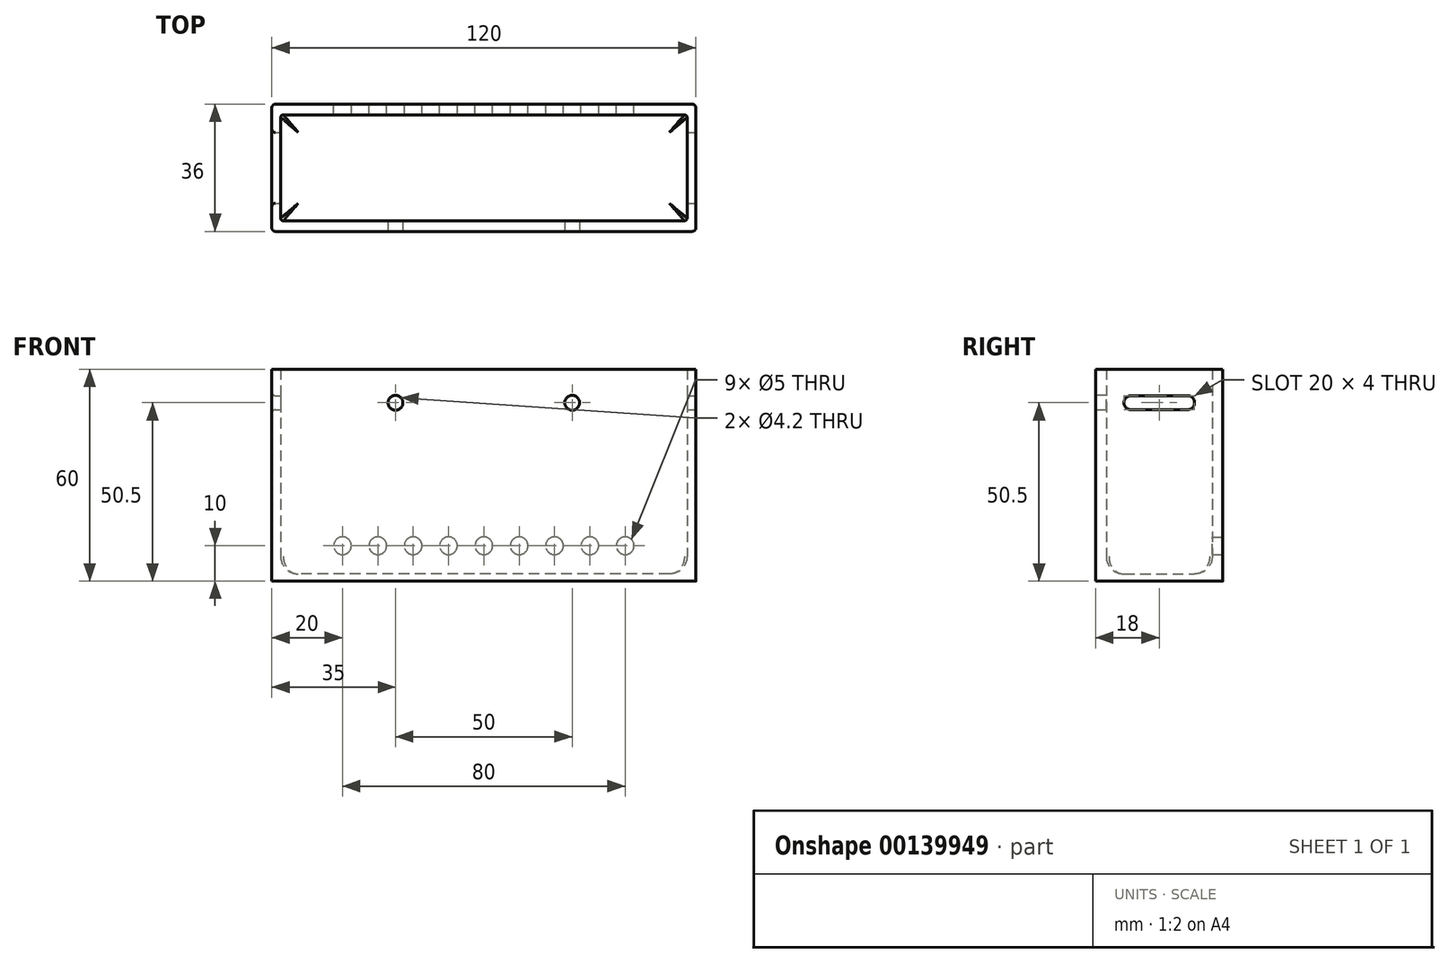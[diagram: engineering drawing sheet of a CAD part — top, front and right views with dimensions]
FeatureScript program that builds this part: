
annotation { "Feature Type Name" : "Feature", "Feature Type Description" : "" }
export const myFeature = defineFeature(function(context is Context, id is Id, definition is map)
    precondition{}
    {
        {
            var Q0;
            Q0=qCreatedBy(makeId("Top.planeOp"),FACE);
            var sketch = newSketch(context, id + "F0", { "sketchPlane" : qUnion([Q0])});
            skLineSegment(sketch, "E0.bottom", {"start": v(0, 0) * mm, "end": v(-115, 0) * mm});
            skLineSegment(sketch, "E0.top", {"start": v(0, 30) * mm, "end": v(-115, 30) * mm});
            skLineSegment(sketch, "E0.left", {"start": v(0, 0) * mm, "end": v(0, 30) * mm});
            skLineSegment(sketch, "E0.right", {"start": v(-115, 0) * mm, "end": v(-115, 30) * mm});
            skLineSegment(sketch, "E1.bottom", {"start": v(-117.5, 33) * mm, "end": v(2.5, 33) * mm});
            skLineSegment(sketch, "E1.top", {"start": v(-117.5, -3) * mm, "end": v(2.5, -3) * mm});
            skLineSegment(sketch, "E1.left", {"start": v(-117.5, 33) * mm, "end": v(-117.5, -3) * mm});
            skLineSegment(sketch, "E1.right", {"start": v(2.5, 33) * mm, "end": v(2.5, -3) * mm});
            skSolve(sketch);
        }
        {
            var Q0;
            Q0=makeQuery(id+"F0.imprint","IMPRINT",FACE,{"disambiguationData":[TD([[makeQuery(id+"F0.imprint","IMPRINT",EDGE,{"derivedFrom":sQuery(id+"F0.wireOp",EDGE,"E0.bottom")}),1.0]])]});
            extrude(context, id + "F1", {"entities" : qUnion([Q0]), "depth" : 60 * mm, "offsetDistance" : 25 * mm});
        }
        {
            var Q0;
            Q0=makeQuery(id+"F0.imprint","IMPRINT",FACE,{"disambiguationData":[TD([[makeQuery(id+"F0.imprint","IMPRINT",EDGE,{"derivedFrom":sQuery(id+"F0.wireOp",EDGE,"E0.bottom")}),-1.0]])]});
            extrude(context, id + "F2", {"entities" : qUnion([Q0]), "operationType" : NewBodyOperationType.ADD, "depth" : 2 * mm, "offsetDistance" : 25 * mm});
        }
        {
            var Q0;
            Q0=makeQuery(id+"F1.opExtrude","SWEPT_FACE",FACE,{"disambiguationData":[OSD([sQuery(id+"F0.wireOp",EDGE,"E1.right")])]});
            var sketch = newSketch(context, id + "F3", { "sketchPlane" : qUnion([Q0])});
            skArc(sketch, "E2", {"start": v(23, 48.5) * mm, "mid": v(25, 50.5) * mm, "end": v(23, 52.5) * mm});
            skArc(sketch, "E3", {"start": v(7, 52.5) * mm, "mid": v(5, 50.5) * mm, "end": v(7, 48.5) * mm});
            skLineSegment(sketch, "E4", {"start": v(23, 52.5) * mm, "end": v(7, 52.5) * mm});
            skLineSegment(sketch, "E5", {"start": v(23, 48.5) * mm, "end": v(7, 48.5) * mm});
            skSolve(sketch);
        }
        {
            var Q0;
            Q0 = qSketchRegion(id + "F3", true);
            extrude(context, id + "F4", {"entities" : qUnion([Q0]), "operationType" : NewBodyOperationType.REMOVE, "oppositeDirection" : true, "depth" : 200 * mm, "offsetDistance" : 25 * mm});
        }
        {
            var Q0;
            Q0=makeQuery(id+"F1.opExtrude","SWEPT_FACE",FACE,{"disambiguationData":[OSD([sQuery(id+"F0.wireOp",EDGE,"E1.bottom")])]});
            var sketch = newSketch(context, id + "F5", { "sketchPlane" : qUnion([Q0])});
            skCircle(sketch, "E6", {"center": v(17.5, 10) * mm, "radius": 2.5 * mm});
            skCircle(sketch, "E7.1.0.0", {"center": v(27.5, 10) * mm, "radius": 2.5 * mm});
            skCircle(sketch, "E7.2.0.0", {"center": v(37.5, 10) * mm, "radius": 2.5 * mm});
            skCircle(sketch, "E7.3.0.0", {"center": v(47.5, 10) * mm, "radius": 2.5 * mm});
            skCircle(sketch, "E7.4.0.0", {"center": v(57.5, 10) * mm, "radius": 2.5 * mm});
            skCircle(sketch, "E7.5.0.0", {"center": v(67.5, 10) * mm, "radius": 2.5 * mm});
            skCircle(sketch, "E7.6.0.0", {"center": v(77.5, 10) * mm, "radius": 2.5 * mm});
            skCircle(sketch, "E7.7.0.0", {"center": v(87.5, 10) * mm, "radius": 2.5 * mm});
            skCircle(sketch, "E7.8.0.0", {"center": v(97.5, 10) * mm, "radius": 2.5 * mm});
            skLineSegment(sketch, "E7.direction1", {"start": v(8, 10) * mm, "end": v(18, 10) * mm, "construction": true});
            skSolve(sketch);
        }
        {
            var Q0;
            Q0 = qSketchRegion(id + "F5", true);
            extrude(context, id + "F6", {"entities" : qUnion([Q0]), "operationType" : NewBodyOperationType.REMOVE, "oppositeDirection" : true, "depth" : 5 * mm, "offsetDistance" : 25 * mm});
        }
        {
            var Q0;
            Q0=makeQuery(id+"F1.opExtrude","SWEPT_FACE",FACE,{"disambiguationData":[OSD([sQuery(id+"F0.wireOp",EDGE,"E1.top")])]});
            var sketch = newSketch(context, id + "F7", { "sketchPlane" : qUnion([Q0])});
            skCircle(sketch, "E8", {"center": v(-82.5, 50.5) * mm, "radius": 2.1 * mm});
            skCircle(sketch, "E9", {"center": v(-32.5, 50.5) * mm, "radius": 2.1 * mm});
            skLineSegment(sketch, "E10", {"start": v(-82.5, 50.5) * mm, "end": v(-117.5, 50.5) * mm, "construction": true});
            skLineSegment(sketch, "E11", {"start": v(-32.5, 50.5) * mm, "end": v(2.5, 50.5) * mm, "construction": true});
            skSolve(sketch);
        }
        {
            var Q0;
            Q0 = qSketchRegion(id + "F7", true);
            extrude(context, id + "F8", {"entities" : qUnion([Q0]), "operationType" : NewBodyOperationType.REMOVE, "oppositeDirection" : true, "depth" : 5 * mm, "offsetDistance" : 25 * mm});
        }
        {
            var Q0;
            Q0=makeQuery(id+"F1.opExtrude","SWEPT_EDGE",EDGE,{"disambiguationData":[OSD([sQuery(id+"F0.wireOp",EDGE,"E1.top"),sQuery(id+"F0.wireOp",EDGE,"E1.left")])]});
            var Q1;
            Q1=makeQuery(id+"F1.opExtrude","SWEPT_EDGE",EDGE,{"disambiguationData":[OSD([sQuery(id+"F0.wireOp",EDGE,"E1.bottom"),sQuery(id+"F0.wireOp",EDGE,"E1.left")])]});
            var Q2;
            Q2=makeQuery(id+"F1.opExtrude","SWEPT_EDGE",EDGE,{"disambiguationData":[OSD([sQuery(id+"F0.wireOp",EDGE,"E1.bottom"),sQuery(id+"F0.wireOp",EDGE,"E1.right")])]});
            var Q3;
            Q3=makeQuery(id+"F1.opExtrude","SWEPT_EDGE",EDGE,{"disambiguationData":[OSD([sQuery(id+"F0.wireOp",EDGE,"E1.top"),sQuery(id+"F0.wireOp",EDGE,"E1.right")])]});
            var Q4;
            Q4=makeQuery(id+"F4.boolean.opBoolean","COPY",EDGE,{"derivedFrom":makeQuery(id+"F4.opExtrude","CAP_EDGE",EDGE,{"disambiguationData":[OSD([sQuery(id+"F3.wireOp",EDGE,"E5")])],"isStart":true})});
            var Q5;
            Q5=makeQuery(id+"F4.boolean.opBoolean","COPY",EDGE,{"derivedFrom":makeQuery(id+"F4.opExtrude","CAP_EDGE",EDGE,{"disambiguationData":[OSD([sQuery(id+"F3.wireOp",EDGE,"E2")])],"isStart":true})});
            var Q6;
            Q6=makeQuery(id+"F4.boolean.opBoolean","COPY",EDGE,{"derivedFrom":makeQuery(id+"F4.opExtrude","CAP_EDGE",EDGE,{"disambiguationData":[OSD([sQuery(id+"F3.wireOp",EDGE,"E4")])],"isStart":true})});
            var Q7;
            Q7=makeQuery(id+"F4.boolean.opBoolean","COPY",EDGE,{"derivedFrom":makeQuery(id+"F4.opExtrude","CAP_EDGE",EDGE,{"disambiguationData":[OSD([sQuery(id+"F3.wireOp",EDGE,"E3")])],"isStart":true})});
            var Q8;
            Q8=makeQuery(id+"F4.boolean.opBoolean","INTERSECT",EDGE,{"derivedFrom":[makeQuery(id+"F1.opExtrude","SWEPT_FACE",FACE,{"disambiguationData":[OSD([sQuery(id+"F0.wireOp",EDGE,"E1.left")])]}),makeQuery(id+"F4.opExtrude","SWEPT_FACE",FACE,{"disambiguationData":[OSD([sQuery(id+"F3.wireOp",EDGE,"E4")])]})]});
            var Q9;
            Q9=makeQuery(id+"F4.boolean.opBoolean","INTERSECT",EDGE,{"derivedFrom":[makeQuery(id+"F1.opExtrude","SWEPT_FACE",FACE,{"disambiguationData":[OSD([sQuery(id+"F0.wireOp",EDGE,"E1.left")])]}),makeQuery(id+"F4.opExtrude","SWEPT_FACE",FACE,{"disambiguationData":[OSD([sQuery(id+"F3.wireOp",EDGE,"E5")])]})]});
            var Q10;
            Q10=makeQuery(id+"F4.boolean.opBoolean","INTERSECT",EDGE,{"derivedFrom":[makeQuery(id+"F1.opExtrude","SWEPT_FACE",FACE,{"disambiguationData":[OSD([sQuery(id+"F0.wireOp",EDGE,"E1.left")])]}),makeQuery(id+"F4.opExtrude","SWEPT_FACE",FACE,{"disambiguationData":[OSD([sQuery(id+"F3.wireOp",EDGE,"E2")])]})]});
            var Q11;
            Q11=makeQuery(id+"F4.boolean.opBoolean","INTERSECT",EDGE,{"derivedFrom":[makeQuery(id+"F1.opExtrude","SWEPT_FACE",FACE,{"disambiguationData":[OSD([sQuery(id+"F0.wireOp",EDGE,"E1.left")])]}),makeQuery(id+"F4.opExtrude","SWEPT_FACE",FACE,{"disambiguationData":[OSD([sQuery(id+"F3.wireOp",EDGE,"E3")])]})]});
            var Q12;
            Q12=makeQuery(id+"F8.boolean.opBoolean","COPY",EDGE,{"derivedFrom":makeQuery(id+"F8.opExtrude","CAP_EDGE",EDGE,{"disambiguationData":[OSD([sQuery(id+"F7.wireOp",EDGE,"E8")])],"isStart":true})});
            var Q13;
            Q13=makeQuery(id+"F8.boolean.opBoolean","COPY",EDGE,{"derivedFrom":makeQuery(id+"F8.opExtrude","CAP_EDGE",EDGE,{"disambiguationData":[OSD([sQuery(id+"F7.wireOp",EDGE,"E9")])],"isStart":true})});
            var Q14;
            Q14=makeQuery(id+"F6.boolean.opBoolean","COPY",EDGE,{"derivedFrom":makeQuery(id+"F6.opExtrude","CAP_EDGE",EDGE,{"disambiguationData":[OSD([sQuery(id+"F5.wireOp",EDGE,"E6")])],"isStart":true})});
            var Q15;
            Q15=makeQuery(id+"F6.boolean.opBoolean","COPY",EDGE,{"derivedFrom":makeQuery(id+"F6.opExtrude","CAP_EDGE",EDGE,{"disambiguationData":[OSD([sQuery(id+"F5.wireOp",EDGE,"E7.1.0.0")])],"isStart":true})});
            var Q16;
            Q16=makeQuery(id+"F6.boolean.opBoolean","COPY",EDGE,{"derivedFrom":makeQuery(id+"F6.opExtrude","CAP_EDGE",EDGE,{"disambiguationData":[OSD([sQuery(id+"F5.wireOp",EDGE,"E7.8.0.0")])],"isStart":true})});
            var Q17;
            Q17=makeQuery(id+"F6.boolean.opBoolean","COPY",EDGE,{"derivedFrom":makeQuery(id+"F6.opExtrude","CAP_EDGE",EDGE,{"disambiguationData":[OSD([sQuery(id+"F5.wireOp",EDGE,"E7.7.0.0")])],"isStart":true})});
            var Q18;
            Q18=makeQuery(id+"F6.boolean.opBoolean","COPY",EDGE,{"derivedFrom":makeQuery(id+"F6.opExtrude","CAP_EDGE",EDGE,{"disambiguationData":[OSD([sQuery(id+"F5.wireOp",EDGE,"E7.6.0.0")])],"isStart":true})});
            var Q19;
            Q19=makeQuery(id+"F6.boolean.opBoolean","COPY",EDGE,{"derivedFrom":makeQuery(id+"F6.opExtrude","CAP_EDGE",EDGE,{"disambiguationData":[OSD([sQuery(id+"F5.wireOp",EDGE,"E7.5.0.0")])],"isStart":true})});
            var Q20;
            Q20=makeQuery(id+"F6.boolean.opBoolean","COPY",EDGE,{"derivedFrom":makeQuery(id+"F6.opExtrude","CAP_EDGE",EDGE,{"disambiguationData":[OSD([sQuery(id+"F5.wireOp",EDGE,"E7.4.0.0")])],"isStart":true})});
            var Q21;
            Q21=makeQuery(id+"F6.boolean.opBoolean","COPY",EDGE,{"derivedFrom":makeQuery(id+"F6.opExtrude","CAP_EDGE",EDGE,{"disambiguationData":[OSD([sQuery(id+"F5.wireOp",EDGE,"E7.3.0.0")])],"isStart":true})});
            var Q22;
            Q22=makeQuery(id+"F6.boolean.opBoolean","COPY",EDGE,{"derivedFrom":makeQuery(id+"F6.opExtrude","CAP_EDGE",EDGE,{"disambiguationData":[OSD([sQuery(id+"F5.wireOp",EDGE,"E7.2.0.0")])],"isStart":true})});
            fillet(context, id + "F9", {"entities" : qUnion([Q0, Q1, Q2, Q3, Q4, Q5, Q6, Q7, Q8, Q9, Q10, Q11, Q12, Q13, Q14, Q15, Q16, Q17, Q18, Q19, Q20, Q21, Q22]), "radius" : 1 * mm, "tangentPropagation" : true, "allowEdgeOverflow" : false});
        }
        {
            var Q0;
            Q0=makeQuery(id+"F1.opExtrude","SWEPT_EDGE",EDGE,{"disambiguationData":[OSD([sQuery(id+"F0.wireOp",EDGE,"E0.top"),sQuery(id+"F0.wireOp",EDGE,"E0.left")])]});
            var Q1;
            Q1=makeQuery(id+"F1.opExtrude","SWEPT_EDGE",EDGE,{"disambiguationData":[OSD([sQuery(id+"F0.wireOp",EDGE,"E0.top"),sQuery(id+"F0.wireOp",EDGE,"E0.right")])]});
            var Q2;
            Q2=makeQuery(id+"F1.opExtrude","SWEPT_EDGE",EDGE,{"disambiguationData":[OSD([sQuery(id+"F0.wireOp",EDGE,"E0.bottom"),sQuery(id+"F0.wireOp",EDGE,"E0.right")])]});
            var Q3;
            Q3=makeQuery(id+"F1.opExtrude","SWEPT_EDGE",EDGE,{"disambiguationData":[OSD([sQuery(id+"F0.wireOp",EDGE,"E0.bottom"),sQuery(id+"F0.wireOp",EDGE,"E0.left")])]});
            fillet(context, id + "F10", {"entities" : qUnion([Q0, Q1, Q2, Q3]), "radius" : 0.75 * mm, "tangentPropagation" : true, "allowEdgeOverflow" : false});
        }
        {
            var Q0;
            Q0=makeQuery(id+"F2.opExtrude","CAP_EDGE",EDGE,{"disambiguationData":[OSD([sQuery(id+"F0.wireOp",EDGE,"E0.right")])],"isStart":false});
            var Q1;
            {var subQ0=sQuery(id+"F0.wireOp",EDGE,"E0.right");var subQ1=sQuery(id+"F0.wireOp",EDGE,"E0.bottom");Q1=makeQuery(id+"F10.opFillet","BLEND_EDGE",EDGE,{"blendedFrom":[makeQuery(id+"F1.opExtrude","SWEPT_EDGE",EDGE,{"disambiguationData":[OSD([subQ1,subQ0])]}),makeQuery(id+"F2.opExtrude","CAP_FACE",FACE,{"disambiguationData":[OSD([subQ1,sQuery(id+"F0.wireOp",EDGE,"E0.top"),sQuery(id+"F0.wireOp",EDGE,"E0.left"),subQ0])],"isStart":false})],"blendedInto":[makeQuery(id+"F2.opExtrude","CAP_FACE",FACE,{"disambiguationData":[OSD([subQ1,sQuery(id+"F0.wireOp",EDGE,"E0.top"),sQuery(id+"F0.wireOp",EDGE,"E0.left"),subQ0])],"isStart":false})]});}
            var Q2;
            Q2=makeQuery(id+"F2.opExtrude","CAP_EDGE",EDGE,{"disambiguationData":[OSD([sQuery(id+"F0.wireOp",EDGE,"E0.bottom")])],"isStart":false});
            var Q3;
            {var subQ0=sQuery(id+"F0.wireOp",EDGE,"E0.right");var subQ1=sQuery(id+"F0.wireOp",EDGE,"E0.top");Q3=makeQuery(id+"F10.opFillet","BLEND_EDGE",EDGE,{"blendedFrom":[makeQuery(id+"F1.opExtrude","SWEPT_EDGE",EDGE,{"disambiguationData":[OSD([subQ1,subQ0])]}),makeQuery(id+"F2.opExtrude","CAP_FACE",FACE,{"disambiguationData":[OSD([sQuery(id+"F0.wireOp",EDGE,"E0.bottom"),subQ1,sQuery(id+"F0.wireOp",EDGE,"E0.left"),subQ0])],"isStart":false})],"blendedInto":[makeQuery(id+"F2.opExtrude","CAP_FACE",FACE,{"disambiguationData":[OSD([sQuery(id+"F0.wireOp",EDGE,"E0.bottom"),subQ1,sQuery(id+"F0.wireOp",EDGE,"E0.left"),subQ0])],"isStart":false})]});}
            var Q4;
            Q4=makeQuery(id+"F2.opExtrude","CAP_EDGE",EDGE,{"disambiguationData":[OSD([sQuery(id+"F0.wireOp",EDGE,"E0.top")])],"isStart":false});
            var Q5;
            {var subQ0=sQuery(id+"F0.wireOp",EDGE,"E0.left");var subQ1=sQuery(id+"F0.wireOp",EDGE,"E0.top");Q5=makeQuery(id+"F10.opFillet","BLEND_EDGE",EDGE,{"blendedFrom":[makeQuery(id+"F1.opExtrude","SWEPT_EDGE",EDGE,{"disambiguationData":[OSD([subQ1,subQ0])]}),makeQuery(id+"F2.opExtrude","CAP_FACE",FACE,{"disambiguationData":[OSD([sQuery(id+"F0.wireOp",EDGE,"E0.bottom"),subQ1,subQ0,sQuery(id+"F0.wireOp",EDGE,"E0.right")])],"isStart":false})],"blendedInto":[makeQuery(id+"F2.opExtrude","CAP_FACE",FACE,{"disambiguationData":[OSD([sQuery(id+"F0.wireOp",EDGE,"E0.bottom"),subQ1,subQ0,sQuery(id+"F0.wireOp",EDGE,"E0.right")])],"isStart":false})]});}
            var Q6;
            Q6=makeQuery(id+"F2.opExtrude","CAP_EDGE",EDGE,{"disambiguationData":[OSD([sQuery(id+"F0.wireOp",EDGE,"E0.left")])],"isStart":false});
            var Q7;
            {var subQ0=sQuery(id+"F0.wireOp",EDGE,"E0.left");var subQ1=sQuery(id+"F0.wireOp",EDGE,"E0.bottom");Q7=makeQuery(id+"F10.opFillet","BLEND_EDGE",EDGE,{"blendedFrom":[makeQuery(id+"F1.opExtrude","SWEPT_EDGE",EDGE,{"disambiguationData":[OSD([subQ1,subQ0])]}),makeQuery(id+"F2.opExtrude","CAP_FACE",FACE,{"disambiguationData":[OSD([subQ1,sQuery(id+"F0.wireOp",EDGE,"E0.top"),subQ0,sQuery(id+"F0.wireOp",EDGE,"E0.right")])],"isStart":false})],"blendedInto":[makeQuery(id+"F2.opExtrude","CAP_FACE",FACE,{"disambiguationData":[OSD([subQ1,sQuery(id+"F0.wireOp",EDGE,"E0.top"),subQ0,sQuery(id+"F0.wireOp",EDGE,"E0.right")])],"isStart":false})]});}
            fillet(context, id + "F11", {"entities" : qUnion([Q0, Q1, Q2, Q3, Q4, Q5, Q6, Q7]), "radius" : 5 * mm, "tangentPropagation" : true, "allowEdgeOverflow" : false});
        }
    });
